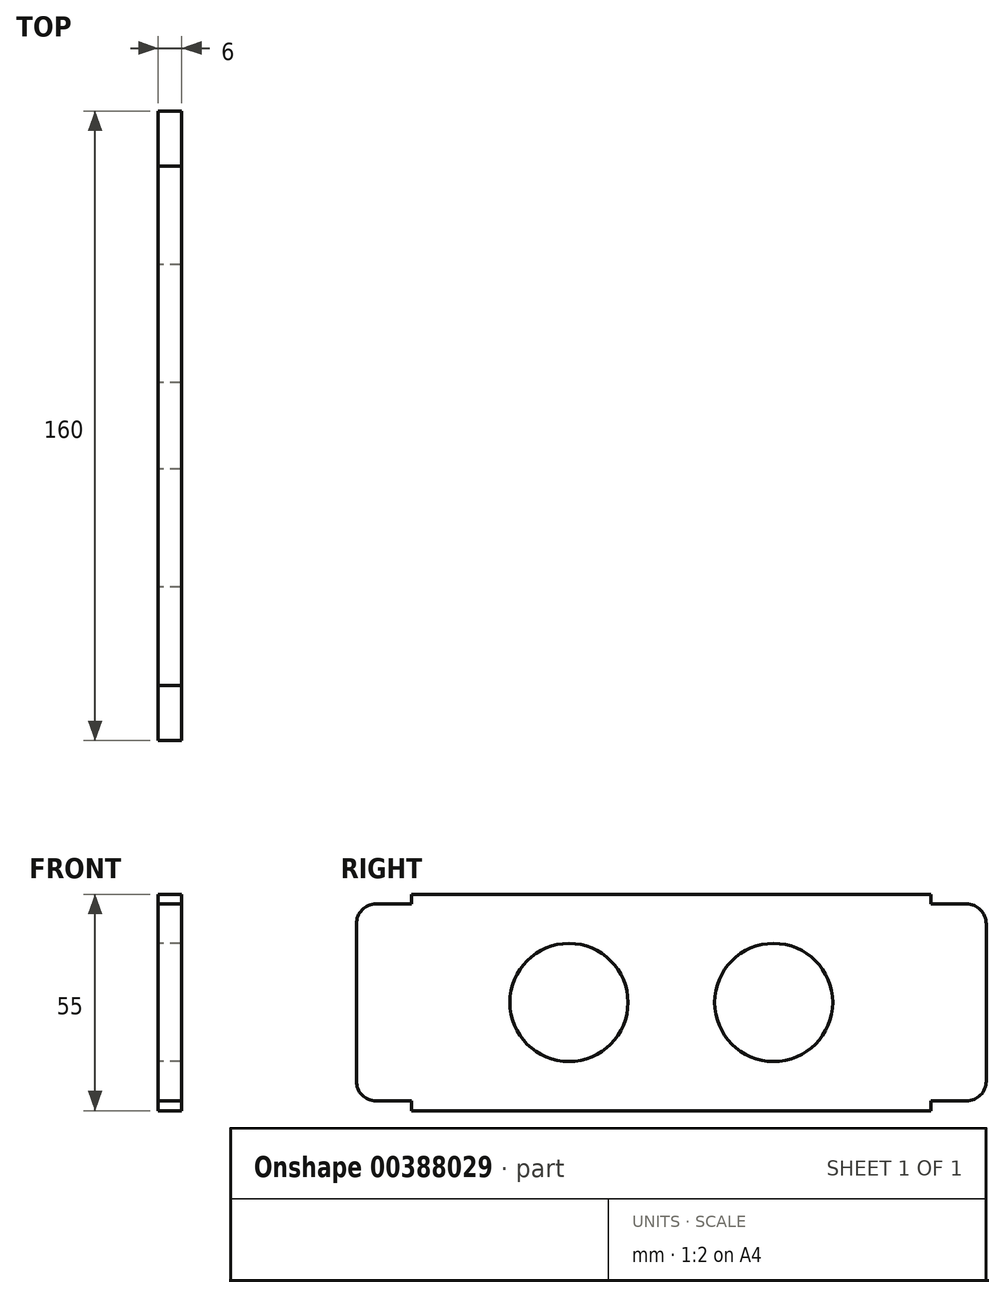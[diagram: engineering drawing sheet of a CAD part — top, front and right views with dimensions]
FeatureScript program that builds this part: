
annotation { "Feature Type Name" : "Feature", "Feature Type Description" : "" }
export const myFeature = defineFeature(function(context is Context, id is Id, definition is map)
    precondition{}
    {
        {
            var Q0;
            Q0=qCreatedBy(makeId("Right.planeOp"),FACE);
            var sketch = newSketch(context, id + "F0", { "sketchPlane" : qUnion([Q0])});
            skLineSegment(sketch, "E0.bottom", {"start": v(0, 55) * mm, "end": v(132, 55) * mm});
            skLineSegment(sketch, "E0.top", {"start": v(0, 0) * mm, "end": v(132, 0) * mm});
            skLineSegment(sketch, "E0.left", {"start": v(0, 55) * mm, "end": v(0, 0) * mm});
            skLineSegment(sketch, "E0.right", {"start": v(132, 55) * mm, "end": v(132, 0) * mm});
            skLineSegment(sketch, "E1.bottom", {"start": v(0, 52.5) * mm, "end": v(-14, 52.5) * mm});
            skLineSegment(sketch, "E1.top", {"start": v(0, 2.5) * mm, "end": v(-14, 2.5) * mm});
            skLineSegment(sketch, "E1.left", {"start": v(0, 52.5) * mm, "end": v(0, 2.5) * mm});
            skLineSegment(sketch, "E1.right", {"start": v(-14, 52.5) * mm, "end": v(-14, 2.5) * mm});
            skLineSegment(sketch, "E2", {"start": v(132, 27.5) * mm, "end": v(-114.92, 27.5) * mm, "construction": true});
            skLineSegment(sketch, "E3", {"start": v(66, 55) * mm, "end": v(66, -51.43) * mm, "construction": true});
            skLineSegment(sketch, "E4.MirrorCS", {"start": v(146, 52.5) * mm, "end": v(146, 2.5) * mm});
            skLineSegment(sketch, "E5.MirrorCS", {"start": v(132, 2.5) * mm, "end": v(146, 2.5) * mm});
            skLineSegment(sketch, "E6.MirrorCS", {"start": v(132, 52.5) * mm, "end": v(146, 52.5) * mm});
            skCircle(sketch, "E7", {"center": v(40, 27.5) * mm, "radius": 15 * mm});
            skCircle(sketch, "E8.MirrorC", {"center": v(92, 27.5) * mm, "radius": 15 * mm});
            skSolve(sketch);
        }
        {
            var Q0;
            Q0 = qSketchRegion(id + "F0", true);
            extrude(context, id + "F1", {"entities" : qUnion([Q0]), "depth" : 6 * mm});
        }
        {
            var Q0;
            Q0=makeQuery(id+"F1.opExtrude","SWEPT_EDGE",EDGE,{"disambiguationData":[OSD([sQuery(id+"F0.wireOp",EDGE,"E1.top"),sQuery(id+"F0.wireOp",EDGE,"E1.right")])]});
            var Q1;
            Q1=makeQuery(id+"F1.opExtrude","SWEPT_EDGE",EDGE,{"disambiguationData":[OSD([sQuery(id+"F0.wireOp",EDGE,"E1.bottom"),sQuery(id+"F0.wireOp",EDGE,"E1.right")])]});
            var Q2;
            Q2=makeQuery(id+"F1.opExtrude","SWEPT_EDGE",EDGE,{"disambiguationData":[OSD([sQuery(id+"F0.wireOp",EDGE,"E4.MirrorCS"),sQuery(id+"F0.wireOp",EDGE,"E6.MirrorCS")])]});
            var Q3;
            Q3=makeQuery(id+"F1.opExtrude","SWEPT_EDGE",EDGE,{"disambiguationData":[OSD([sQuery(id+"F0.wireOp",EDGE,"E4.MirrorCS"),sQuery(id+"F0.wireOp",EDGE,"E5.MirrorCS")])]});
            fillet(context, id + "F2", {"entities" : qUnion([Q0, Q1, Q2, Q3]), "radius" : 5 * mm, "tangentPropagation" : true, "allowEdgeOverflow" : false});
        }
    });
